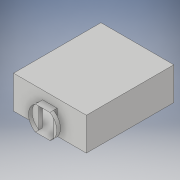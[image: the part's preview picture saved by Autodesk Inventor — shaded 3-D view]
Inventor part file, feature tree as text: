
AUTODESK INVENTOR PART (.ipt)
format: ipt  version: 2017 (Build 210142000, 142)  size: 165,376 bytes
history: native  units: in
note: dims shown in document units (in); Inventor stores cm internally (conversion verified against a paired STEP export)
features: extrude x5, sketch x5, delete_face x1
ambient origin geometry x8: Origin, YZ Plane, XZ Plane, XY Plane, X Axis, Y Axis, Z Axis, Center Point
bodies: Solid1 (feature_tree)
feature tree (11):
  extrude  "floor"  Depth=22.0in
  extrude  "walls"  Depth=1.0in
  extrude  "doorframe"  Depth=1.0in
  extrude  "ceiling"  Depth=1.0in TaperAngle=0.0deg
  extrude  "connection"  Depth=6.6667in
  delete_face  "Delete Face2"
  sketch  "Sketch1"  dims[d0=22.0in d1=26.0in]
  sketch  "Sketch4"  dims[d2=1.0in d3=0.0in d11=1.0in]
  sketch  "Sketch5"  dims[d12=1.0in d13=1.0in]
  sketch  "Sketch7"  dims[d14=1.0in d15=10.0in d16=0.0in]
  sketch  "Sketch12"  dims[d17=2.0in d18=6.6667in d20=8.6667in d21=0.0in d22=1.0in d23=0.0in d37=6.6667in d79=4.0in d80=3.8873in d81=3.8873in d82=1.6458in d83=3.3333in d84=1.0in d85=1.0in d86=1.0in d87=1.0in d88=0.0in]
